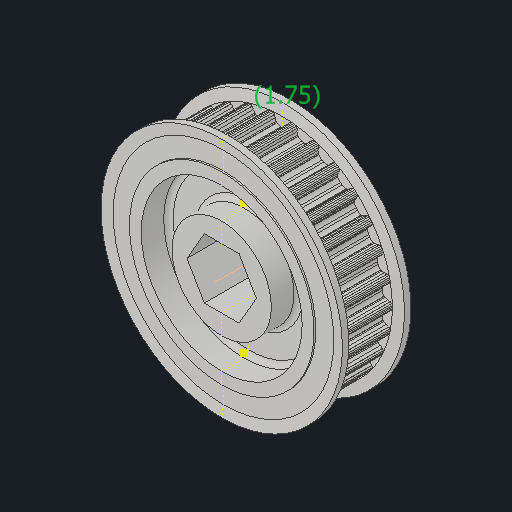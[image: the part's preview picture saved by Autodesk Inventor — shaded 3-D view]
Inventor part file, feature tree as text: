
AUTODESK INVENTOR PART (.ipt)
format: ipt  version: 2023.4 (Build 274418000, 418)  size: 1,121,792 bytes
history: native  units: in
note: dims shown in document units (in); Inventor stores cm internally (conversion verified against a paired STEP export)
features: sketch x1, mirror x1, projected_geometry x1
ambient origin geometry x8: Origin, YZ Plane, XZ Plane, XY Plane, X Axis, Y Axis, Z Axis, Center Point
bodies: Solid1 (feature_tree)
feature tree (3):
  sketch  "Sketch1"  dims[d0=0.0689in]
  mirror  "Mirror1"
  projected_geometry  "Project Cut Edges1"
